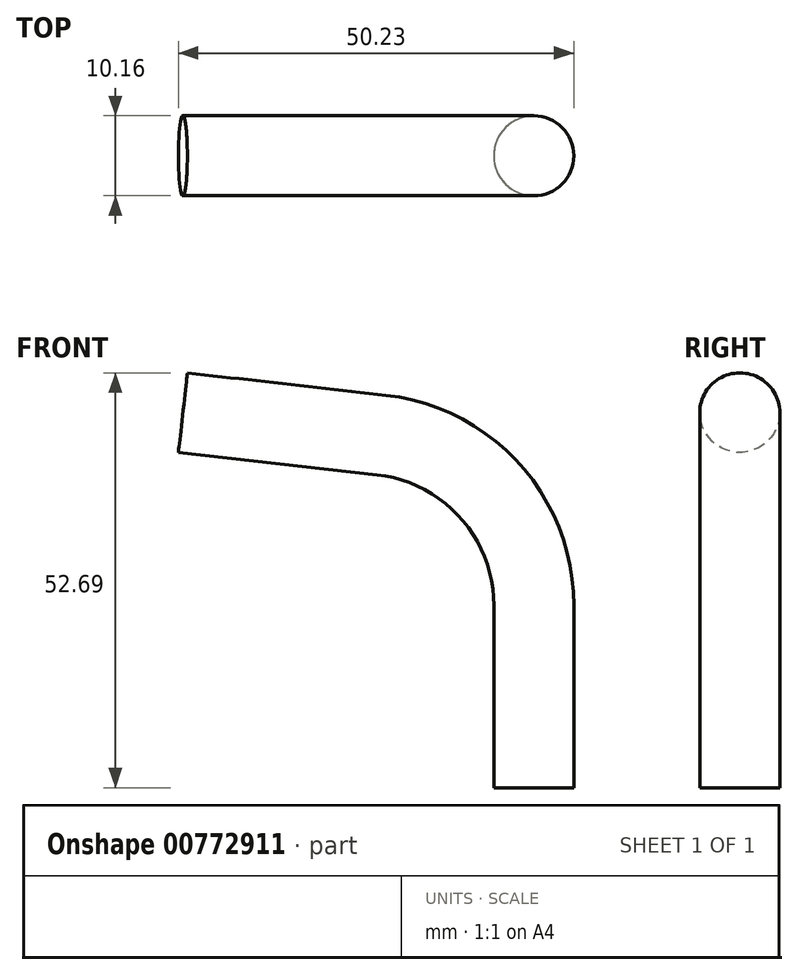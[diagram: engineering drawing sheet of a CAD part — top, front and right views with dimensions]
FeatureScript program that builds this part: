
annotation { "Feature Type Name" : "Feature", "Feature Type Description" : "" }
export const myFeature = defineFeature(function(context is Context, id is Id, definition is map)
    precondition{}
    {
        {
            var Q0;
            Q0=qCreatedBy(makeId("Front.planeOp"),FACE);
            var sketch = newSketch(context, id + "F0", { "sketchPlane" : qUnion([Q0])});
            skLineSegment(sketch, "E0", {"start": v(-24.83, 0) * mm, "end": v(-24.83, 23.14) * mm});
            skArc(sketch, "E1", {"start": v(-24.83, 23.14) * mm, "mid": v(-30.37, 37.66) * mm, "end": v(-44.17, 44.8) * mm});
            skSolve(sketch);
        }
        {
            var Q0;
            Q0=qCreatedBy(makeId("Top.planeOp"),FACE);
            var sketch = newSketch(context, id + "F1", { "sketchPlane" : qUnion([Q0])});
            skCircle(sketch, "E2", {"center": v(-24.83, 0) * mm, "radius": 5.08 * mm});
            skSolve(sketch);
        }
        {
            var Q0;
            Q0=makeQuery(id+"F1.imprint","IMPRINT",FACE,{"disambiguationData":[TD([[makeQuery(id+"F1.imprint","IMPRINT",EDGE,{"derivedFrom":sQuery(id+"F1.wireOp",EDGE,"E2")}),1.0]])]});
            var Q1;
            Q1 = qConstructionFilter(qBodyType(qCreatedBy(id + "F0" ,EDGE), BodyType.WIRE), ConstructionObject.NO);
            sweep(context, id + "F2", {"profiles" : qUnion([Q0]), "path" : qUnion([Q1])});
        }
        {
            var Q0;
            Q0=makeQuery(id+"F2.opSweep","CAP_FACE",FACE,{"disambiguationData":[OSD([sQuery(id+"F0.wireOp",VERTEX,"E1.end"),sQuery(id+"F1.wireOp",EDGE,"E2")])],"isStart":false});
            var sketch = newSketch(context, id + "F3", { "sketchPlane" : qUnion([Q0])});
            skSolve(sketch);
        }
        {
            var Q0;
            Q0=makeQuery(id+"F3.imprint","IMPRINT",FACE,{"disambiguationData":[TD([[makeQuery(id+"F3.imprint","IMPRINT",EDGE,{"derivedFrom":makeQuery(id+"F2.opSweep","CAP_EDGE",EDGE,{"disambiguationData":[OSD([sQuery(id+"F0.wireOp",VERTEX,"E1.end"),sQuery(id+"F1.wireOp",EDGE,"E2")])],"isStart":false})}),1.0]])]});
            extrude(context, id + "F4", {"entities" : qUnion([Q0]), "operationType" : NewBodyOperationType.ADD, "depth" : 25.4 * mm, "offsetDistance" : 25.4 * mm});
        }
    });
